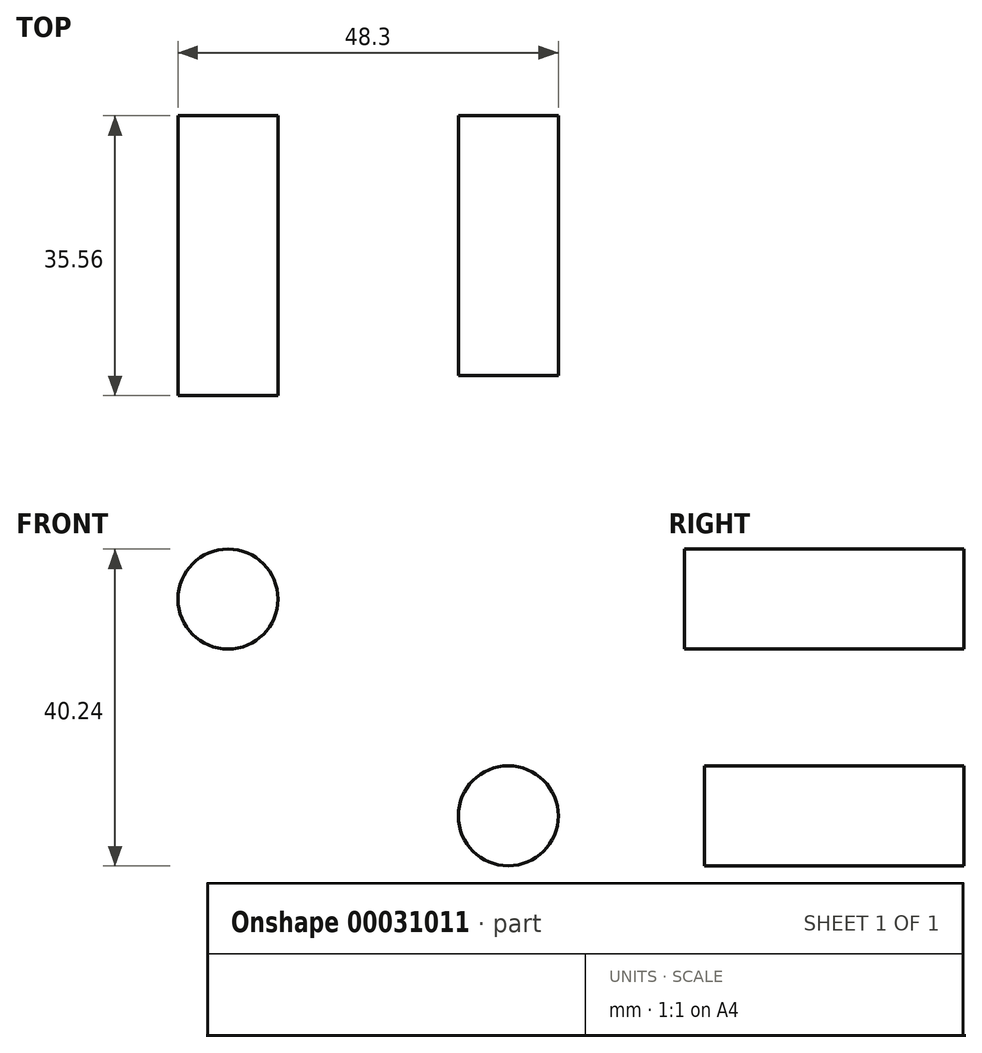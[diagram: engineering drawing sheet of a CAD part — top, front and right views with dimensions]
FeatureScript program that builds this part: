
annotation { "Feature Type Name" : "Feature", "Feature Type Description" : "" }
export const myFeature = defineFeature(function(context is Context, id is Id, definition is map)
    precondition{}
    {
        {
            var Q0;
            Q0=qCreatedBy(makeId("Front.planeOp"),FACE);
            var sketch = newSketch(context, id + "F0", { "sketchPlane" : qUnion([Q0])});
            skCircle(sketch, "E0", {"center": v(0, 0) * mm, "radius": 6.35 * mm});
            skCircle(sketch, "E1", {"center": v(-35.6, 27.54) * mm, "radius": 6.35 * mm});
            skSolve(sketch);
        }
        {
            var Q0;
            Q0=makeQuery(id+"F0.imprint","IMPRINT",FACE,{"disambiguationData":[TD([[makeQuery(id+"F0.imprint","IMPRINT",EDGE,{"derivedFrom":sQuery(id+"F0.wireOp",EDGE,"E0")}),1.0]])]});
            var Q1;
            Q1=makeQuery(id+"F0.imprint","IMPRINT",FACE,{"disambiguationData":[TD([[makeQuery(id+"F0.imprint","IMPRINT",EDGE,{"derivedFrom":sQuery(id+"F0.wireOp",EDGE,"E1")}),1.0]])]});
            extrude(context, id + "F1", {"entities" : qUnion([Q0, Q1]), "depth" : 33.02 * mm});
        }
        {
            var Q0;
            Q0=makeQuery(id+"F1.opExtrude","CAP_FACE",FACE,{"disambiguationData":[OSD([sQuery(id+"F0.wireOp",EDGE,"E1")])],"isStart":false});
            var sketch = newSketch(context, id + "F2", { "sketchPlane" : qUnion([Q0])});
            skCircle(sketch, "E2", {"center": v(-35.6, 27.54) * mm, "radius": 6.35 * mm});
            skSolve(sketch);
        }
        {
            var Q0;
            Q0=makeQuery(id+"F2.imprint","IMPRINT",FACE,{"disambiguationData":[TD([[makeQuery(id+"F2.imprint","IMPRINT",EDGE,{"derivedFrom":sQuery(id+"F2.wireOp",EDGE,"E2")}),1.0]])]});
            extrude(context, id + "F3", {"entities" : qUnion([Q0]), "operationType" : NewBodyOperationType.ADD, "depth" : 2.54 * mm});
        }
    });
